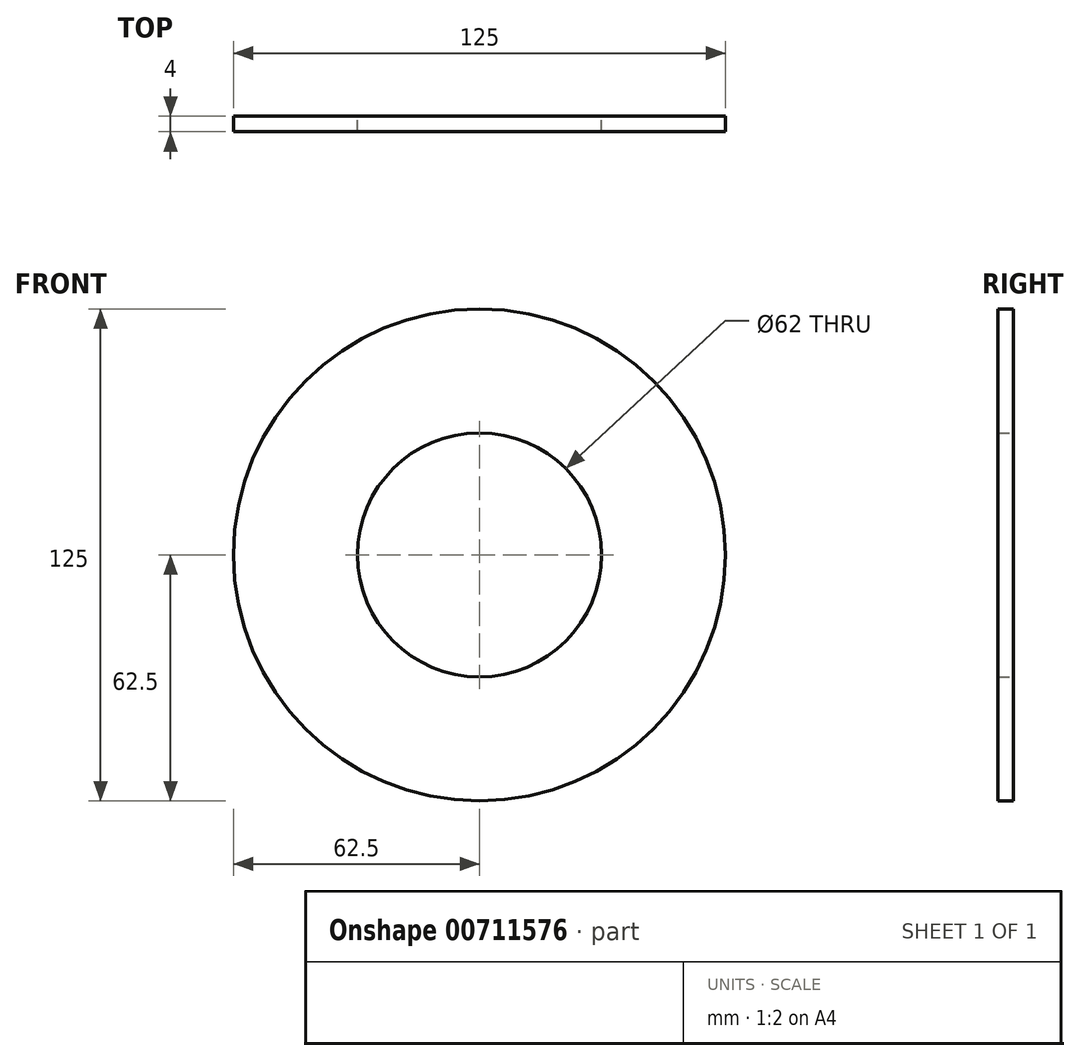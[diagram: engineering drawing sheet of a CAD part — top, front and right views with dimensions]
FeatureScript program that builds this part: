
annotation { "Feature Type Name" : "Feature", "Feature Type Description" : "" }
export const myFeature = defineFeature(function(context is Context, id is Id, definition is map)
    precondition{}
    {
        {
            var Q0;
            Q0=qCreatedBy(makeId("Front.planeOp"),FACE);
            var sketch = newSketch(context, id + "F0", { "sketchPlane" : qUnion([Q0])});
            skCircle(sketch, "E0", {"center": v(0, 0) * mm, "radius": 31 * mm});
            skCircle(sketch, "E1", {"center": v(0, 0) * mm, "radius": 62.5 * mm});
            skSolve(sketch);
        }
        {
            var Q0;
            Q0=makeQuery(id+"F0.imprint","IMPRINT",FACE,{"disambiguationData":[TD([[makeQuery(id+"F0.imprint","IMPRINT",EDGE,{"derivedFrom":sQuery(id+"F0.wireOp",EDGE,"E0")}),-1.0]])]});
            extrude(context, id + "F1", {"entities" : qUnion([Q0]), "depth" : 4 * mm, "offsetDistance" : 25 * mm});
        }
    });
